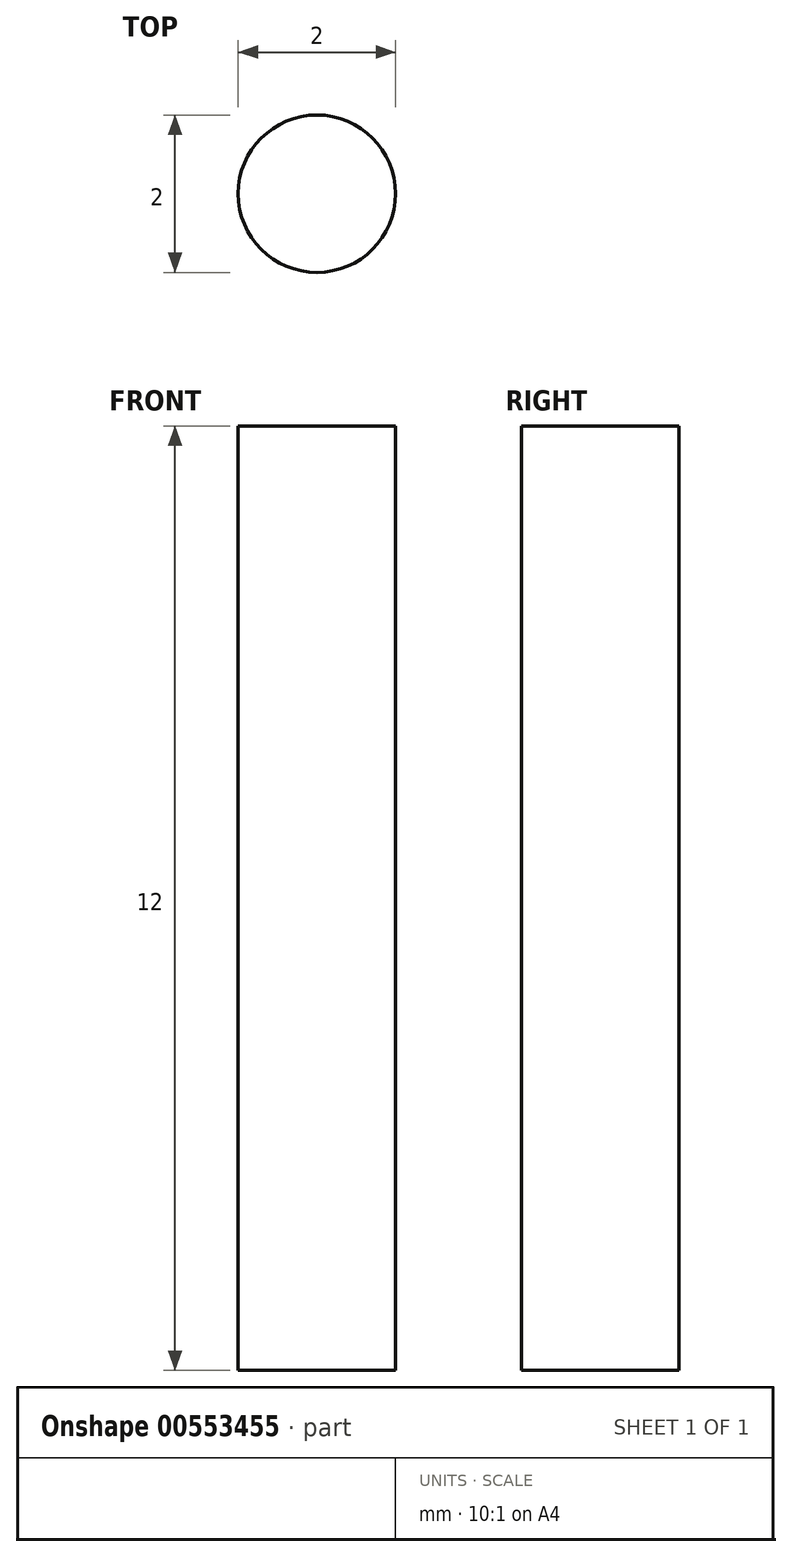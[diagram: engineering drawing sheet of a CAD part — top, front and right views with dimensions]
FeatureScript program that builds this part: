
annotation { "Feature Type Name" : "Feature", "Feature Type Description" : "" }
export const myFeature = defineFeature(function(context is Context, id is Id, definition is map)
    precondition{}
    {
        {
            var Q0;
            Q0=qCreatedBy(makeId("Top.planeOp"),FACE);
            var sketch = newSketch(context, id + "F0", { "sketchPlane" : qUnion([Q0])});
            skCircle(sketch, "E0", {"center": v(0, 0) * mm, "radius": 1 * mm});
            skSolve(sketch);
        }
        {
            var Q0;
            Q0 = qSketchRegion(id + "F0", true);
            extrude(context, id + "F1", {"entities" : qUnion([Q0]), "depth" : 12 * mm, "offsetDistance" : 25 * mm});
        }
    });
